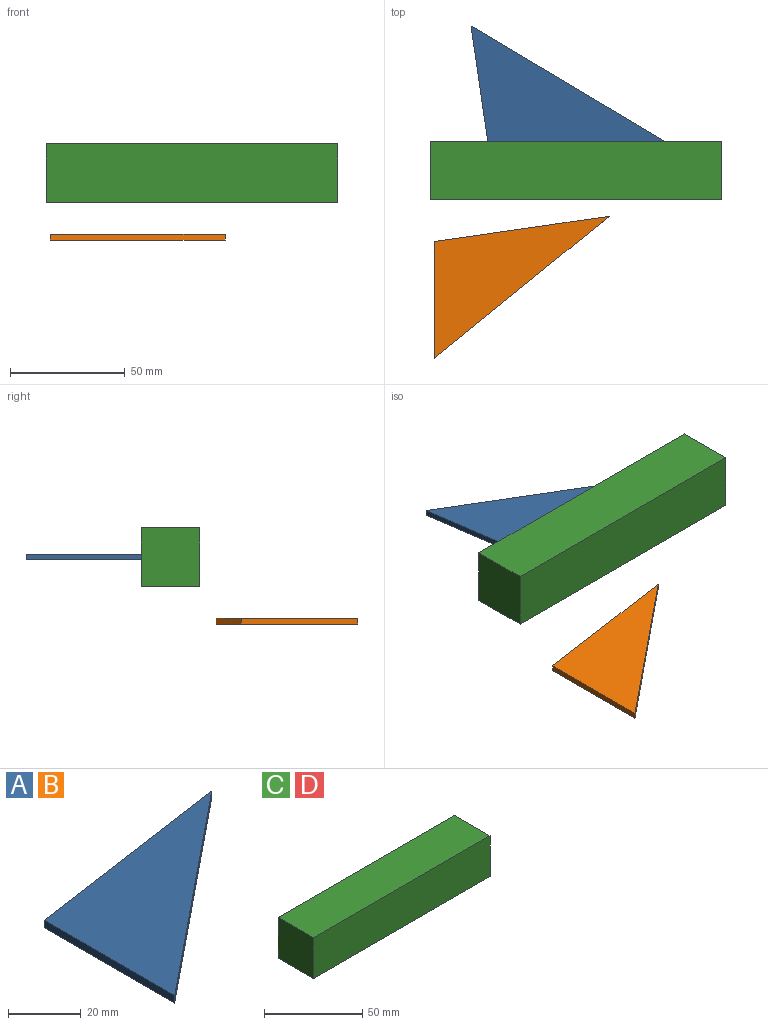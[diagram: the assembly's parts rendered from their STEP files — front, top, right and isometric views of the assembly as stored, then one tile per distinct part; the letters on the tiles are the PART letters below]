
ASSEMBLY  parts=4 mates=1
PART A: 5 faces, bbox 76.2x61.8x2.5 mm
  f0: plane 76.2x11.02mm, normal (-0.14,0.99,0), area 195.6mm2, adj f1,f2,f3,f4
  f1: plane 50.8x2.54mm, normal (-1,0,0), area 129mm2, adj f0,f2,f3,f4
  f2: plane 76.2x61.82mm, normal (0.63,-0.78,0), area 249.2mm2, adj f0,f1,f3,f4
  f3: plane 76.2x61.82mm, normal (0,0,1), area 1935.5mm2, adj f0,f1,f2
  f4: plane 76.2x61.82mm, normal (0,0,-1), area 1935.5mm2, adj f0,f1,f2
PART B: same geometry as A
PART C: 6 faces, bbox 127x25.4x25.4 mm
  f0: plane 127x25.4mm, normal (0,1,0), area 3225.8mm2, adj f1,f3,f4,f5
  f1: plane 25.4x25.4mm, normal (-1,0,0), area 645.2mm2, adj f0,f2,f4,f5
  f2: plane 127x25.4mm, normal (0,-1,0), area 3225.8mm2, adj f1,f3,f4,f5
  f3: plane 25.4x25.4mm, normal (1,0,0), area 645.2mm2, adj f0,f2,f4,f5
  f4: plane 127x25.4mm, normal (0,0,1), area 3225.8mm2, adj f0,f1,f2,f3
  f5: plane 127x25.4mm, normal (0,0,-1), area 3225.8mm2, adj f0,f1,f2,f3
PART D: same geometry as C
PLACE A rot(axis=(1,0.07,0),180deg) t=(-64.59,12.54,11.48)mm
PLACE B t=(-85.61,-62.11,-19.02)mm
PLACE C t=(-10.88,24.19,-2.49)mm
PLACE D t=(-10.88,24.19,-2.49)mm
MATE fastened A.f0 <-> C.f0  axis (0,-1,0) through (-40.83,-4.07,10.21)mm
